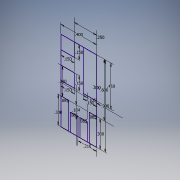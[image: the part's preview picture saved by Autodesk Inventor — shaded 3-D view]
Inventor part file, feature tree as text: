
AUTODESK INVENTOR PART (.ipt)
format: ipt  version: 2018 (Build 220112000, 112)  size: 111,616 bytes
history: native  units: in
note: dims shown in document units (in); Inventor stores cm internally (conversion verified against a paired STEP export)
features: sketch x1
ambient origin geometry x8: Origin, YZ Plane, XZ Plane, XY Plane, X Axis, Y Axis, Z Axis, Center Point
feature tree (1):
  sketch  "Sketch1"  dims[d16=0.4in d17=0.9in d18=0.3in d20=0.085in d21=0.085in d22=0.085in d23=0.085in d24=0.105in d25=0.21in d26=0.1035in d27=0.3in d28=0.15in d29=0.15in d30=0.15in d31=0.15in d32=0.15in d33=0.45in d34=0.0in d35=0.25in d36=0.5998in d37=0.3in]
